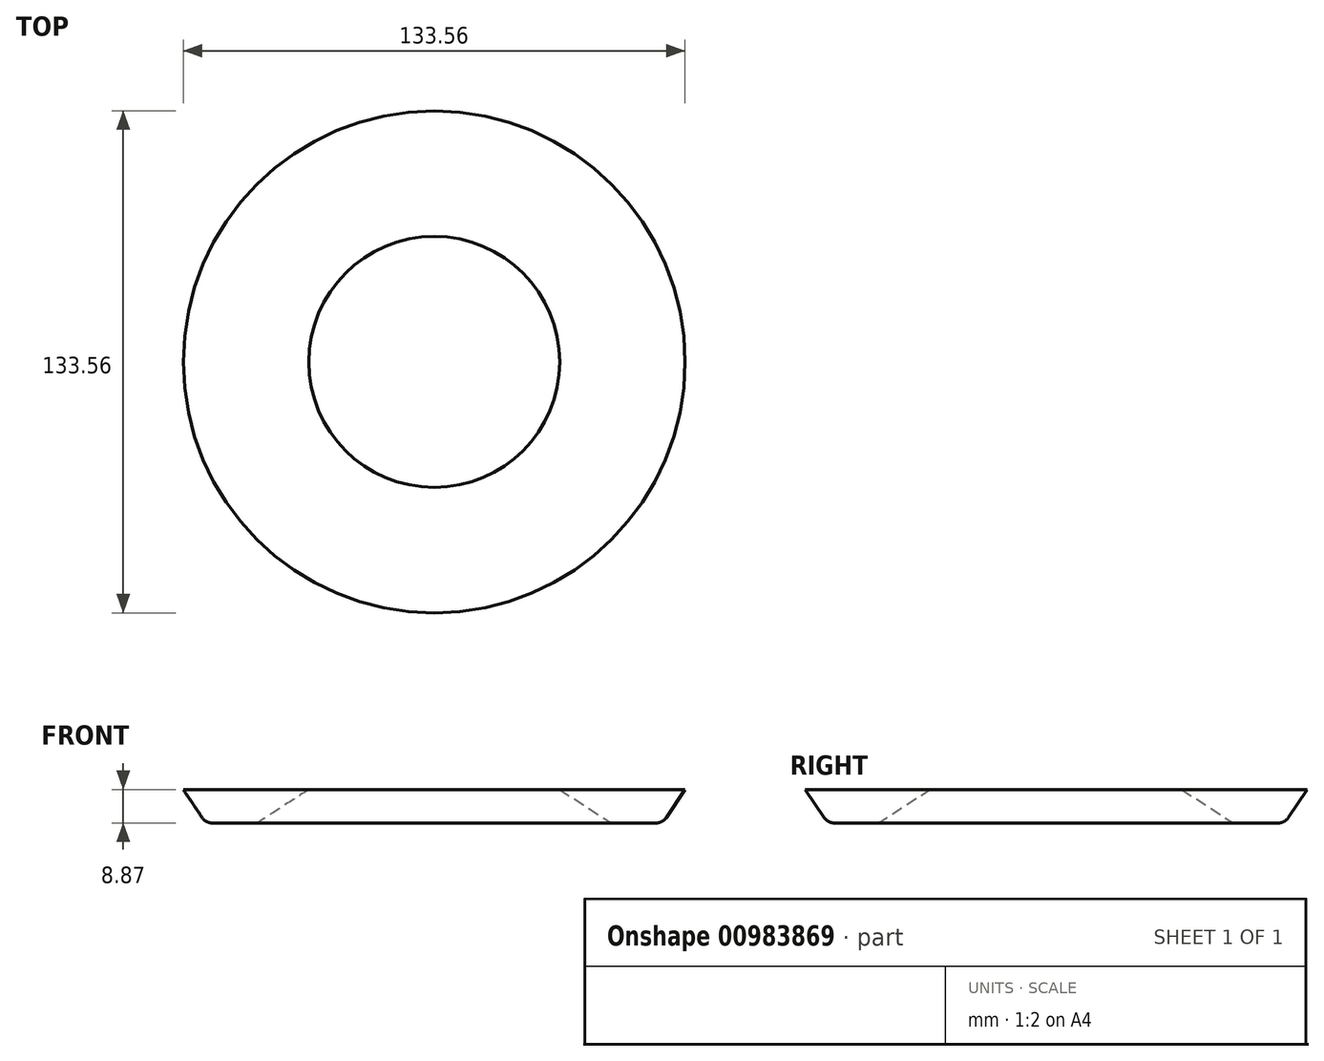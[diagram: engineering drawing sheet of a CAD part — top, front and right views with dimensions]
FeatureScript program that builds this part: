
annotation { "Feature Type Name" : "Feature", "Feature Type Description" : "" }
export const myFeature = defineFeature(function(context is Context, id is Id, definition is map)
    precondition{}
    {
        {
            var Q0;
            Q0=qCreatedBy(makeId("Right.planeOp"),FACE);
            var sketch = newSketch(context, id + "F0", { "sketchPlane" : qUnion([Q0])});
            skLineSegment(sketch, "E0", {"start": v(0, 0) * mm, "end": v(-66.78, 0) * mm});
            skLineSegment(sketch, "E1", {"start": v(-66.78, 0) * mm, "end": v(-61.75, -7.47) * mm});
            skLineSegment(sketch, "E2", {"start": v(-59.11, -8.87) * mm, "end": v(-48.07, -8.87) * mm});
            skLineSegment(sketch, "E3", {"start": v(-46.34, -8.37) * mm, "end": v(-33.39, 0) * mm});
            skPoint(sketch, "E4.visualSharp", {"position": v(-47.13, -8.87) * mm});
            skArc(sketch, "E4.filletArc", {"start": v(-48.07, -8.87) * mm, "mid": v(-47.17, -8.74) * mm, "end": v(-46.34, -8.37) * mm});
            skPoint(sketch, "E5.visualSharp", {"position": v(-60.8, -8.87) * mm});
            skArc(sketch, "E5.filletArc", {"start": v(-61.75, -7.47) * mm, "mid": v(-60.6, -8.5) * mm, "end": v(-59.11, -8.87) * mm});
            skLineSegment(sketch, "E6", {"start": v(0, 0) * mm, "end": v(0, 3.3) * mm});
            skSolve(sketch);
        }
        {
            var Q0;
            Q0 = qSketchRegion(id + "F0", true);
            var Q1;
            Q1=sQuery(id+"F0.wireOp",EDGE,"E6");
            revolve(context, id + "F1", {"surfaceOperationType" : NewSurfaceOperationType.NEW, "entities" : qUnion([Q0]), "axis" : qUnion([Q1]), "revolveType" : RevolveType.FULL});
        }
    });
